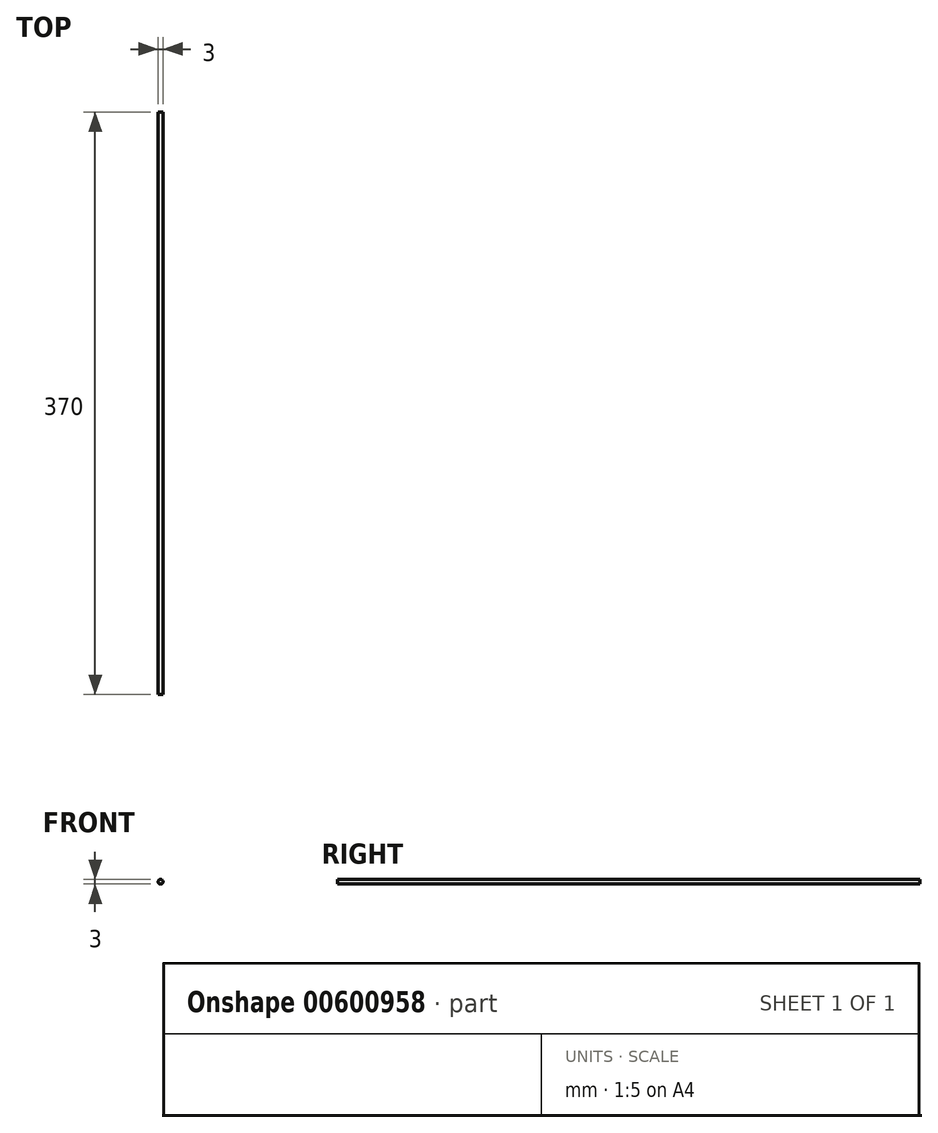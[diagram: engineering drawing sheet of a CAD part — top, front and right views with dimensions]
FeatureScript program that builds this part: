
annotation { "Feature Type Name" : "Feature", "Feature Type Description" : "" }
export const myFeature = defineFeature(function(context is Context, id is Id, definition is map)
    precondition{}
    {
        {
            var Q0;
            Q0=qCreatedBy(makeId("Front.planeOp"),FACE);
            var sketch = newSketch(context, id + "F0", { "sketchPlane" : qUnion([Q0])});
            skCircle(sketch, "E0", {"center": v(0, 0) * mm, "radius": 1.5 * mm});
            skSolve(sketch);
        }
        {
            var Q0;
            Q0=makeQuery(id+"F0.imprint","IMPRINT",FACE,{"disambiguationData":[TD([[makeQuery(id+"F0.imprint","IMPRINT",EDGE,{"derivedFrom":sQuery(id+"F0.wireOp",EDGE,"E0")}),1.0]])]});
            extrude(context, id + "F1", {"entities" : qUnion([Q0]), "depth" : 370 * mm, "offsetDistance" : 25 * mm});
        }
    });
